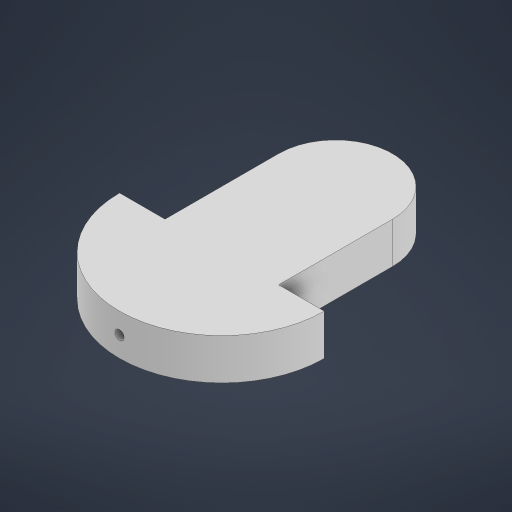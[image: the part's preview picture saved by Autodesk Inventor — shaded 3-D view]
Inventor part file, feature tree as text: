
AUTODESK INVENTOR PART (.ipt)
format: ipt  version: 2024 (Build 280153000, 153)  size: 184,832 bytes
history: native  units: mm
features: extrude x3, sketch x3, other x1, plane x1
ambient origin geometry x8: Origin, YZ Plane, XZ Plane, XY Plane, X Axis, Y Axis, Z Axis, Center Point
bodies: Body1 (feature_tree)
feature tree (8):
  other  "Sólido1"
  extrude  "Extrusión1"  Depth=90.0mm
  plane  "Plano de trabajo2"
  extrude  "Extrusión3"  Depth=4.0mm
  extrude  "Extrusión4"  Depth=2.0mm TaperAngle=0.0deg
  sketch  "Boceto1"  dims[d3=50.0mm d4=90.0mm]
  sketch  "Boceto3"  dims[d7=18.0mm d8=0.0mm d13=4.0mm]
  sketch  "Boceto4"  dims[d14=9.0mm d15=2.0mm d16=0.0mm d17=4.0mm d18=157.75mm d19=0.0mm]
